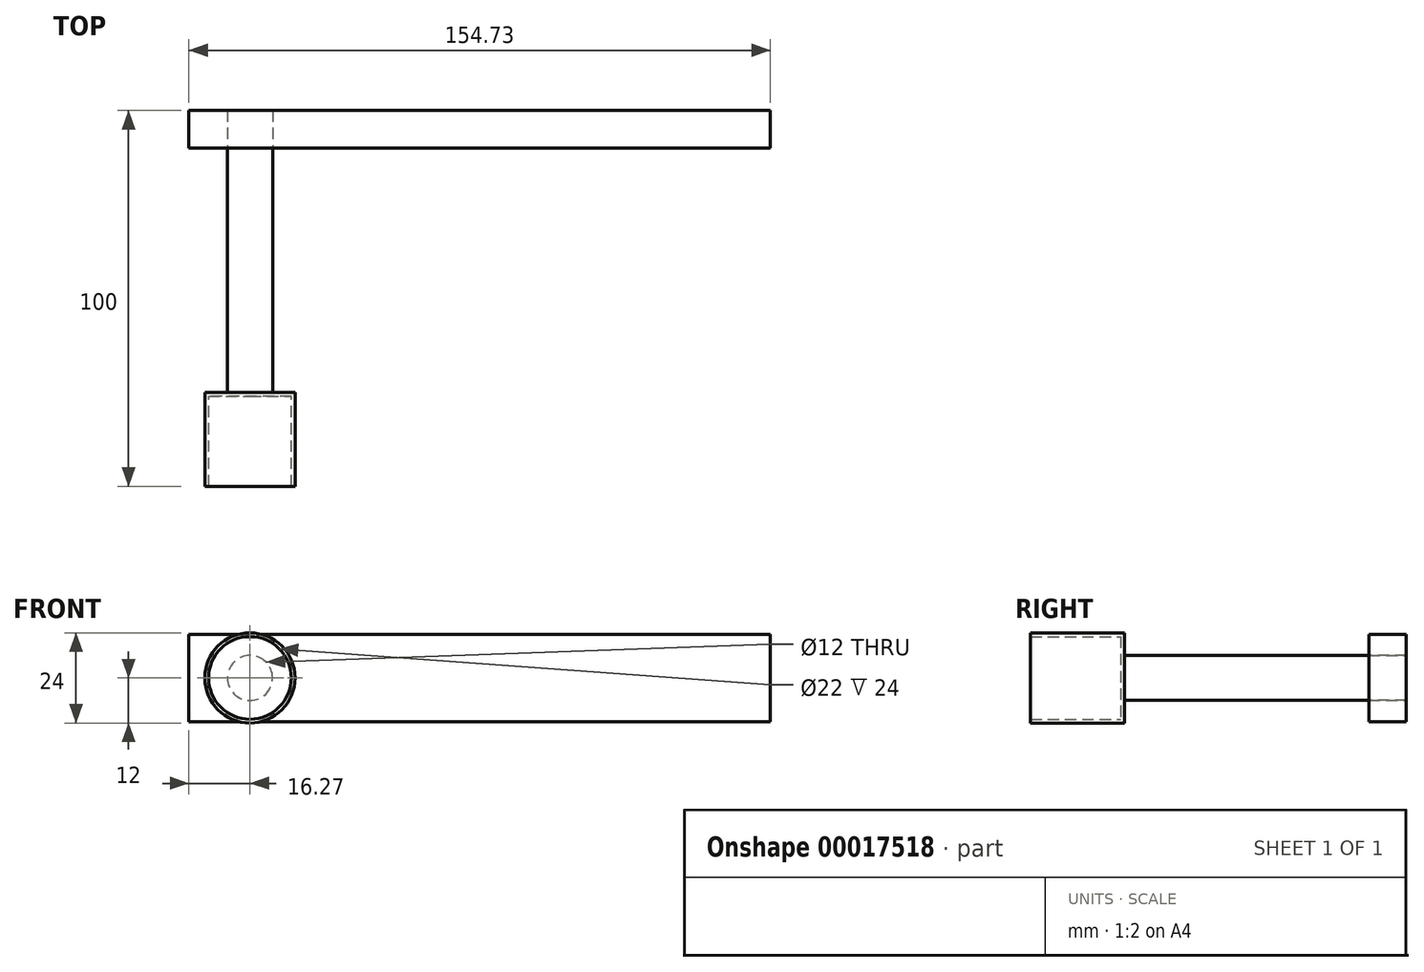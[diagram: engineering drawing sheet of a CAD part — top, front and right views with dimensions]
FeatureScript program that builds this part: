
annotation { "Feature Type Name" : "Feature", "Feature Type Description" : "" }
export const myFeature = defineFeature(function(context is Context, id is Id, definition is map)
    precondition{}
    {
        {
            var Q0;
            Q0=qCreatedBy(makeId("Right.planeOp"),FACE);
            var sketch = newSketch(context, id + "F0", { "sketchPlane" : qUnion([Q0])});
            skLineSegment(sketch, "E0", {"start": v(0, 12) * mm, "end": v(25, 12) * mm});
            skLineSegment(sketch, "E1", {"start": v(25, 12) * mm, "end": v(25, 6) * mm});
            skLineSegment(sketch, "E2", {"start": v(25, 6) * mm, "end": v(100, 6) * mm});
            skLineSegment(sketch, "E3", {"start": v(100, 6) * mm, "end": v(100, 0) * mm});
            skLineSegment(sketch, "E4", {"start": v(100, 0) * mm, "end": v(24, 0) * mm});
            skLineSegment(sketch, "E5", {"start": v(24, 0) * mm, "end": v(24, 11) * mm});
            skLineSegment(sketch, "E6", {"start": v(24, 11) * mm, "end": v(0, 11) * mm});
            skLineSegment(sketch, "E7", {"start": v(0, 12) * mm, "end": v(0, 11) * mm});
            skSolve(sketch);
        }
        {
            var Q0;
            Q0 = qSketchRegion(id + "F0", true);
            var Q1;
            Q1=sQuery(id+"F0.wireOp",EDGE,"E4");
            revolve(context, id + "F1", {"entities" : qUnion([Q0]), "axis" : qUnion([Q1]), "revolveType" : RevolveType.FULL});
        }
        {
            var Q0;
            Q0=qCreatedBy(makeId("Front.planeOp"),FACE);
            cPlane(context, id + "F2", {"entities" : qUnion([Q0]), "cplaneType" : CPlaneType.OFFSET, "offset" : 90 * mm, "oppositeDirection" : true, "width" : 150 * mm, "height" : 150 * mm});
        }
        {
            var Q0;
            Q0=qCreatedBy(id+"F2.planeOp",FACE);
            var sketch = newSketch(context, id + "F3", { "sketchPlane" : qUnion([Q0])});
            skCircle(sketch, "E8.0", {"center": v(0, 0) * mm, "radius": 6 * mm});
            skLineSegment(sketch, "E9.bottom", {"start": v(-16.27, 11.61) * mm, "end": v(138.46, 11.61) * mm});
            skLineSegment(sketch, "E9.top", {"start": v(-16.27, -11.61) * mm, "end": v(138.46, -11.61) * mm});
            skLineSegment(sketch, "E9.left", {"start": v(-16.27, 11.61) * mm, "end": v(-16.27, -11.61) * mm});
            skLineSegment(sketch, "E9.right", {"start": v(138.46, 11.61) * mm, "end": v(138.46, -11.61) * mm});
            skPoint(sketch, "E9.middle", {"position": v(61.1, 0) * mm});
            skSolve(sketch);
        }
        {
            var Q0;
            Q0 = qSketchRegion(id + "F3", true);
            extrude(context, id + "F4", {"entities" : qUnion([Q0]), "oppositeDirection" : true, "depth" : 10 * mm});
        }
    });
